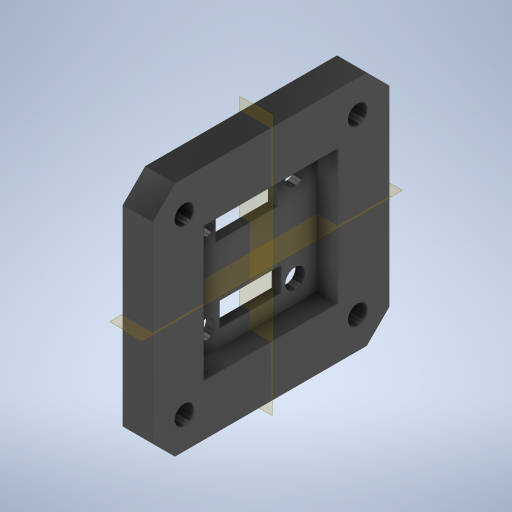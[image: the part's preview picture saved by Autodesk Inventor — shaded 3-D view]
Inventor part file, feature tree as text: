
AUTODESK INVENTOR PART (.ipt)
format: ipt  version: 2023 (Build 270158000, 158)  size: 315,392 bytes
history: native  units: mm
features: sketch x6, extrude x4, hole x2, chamfer x1
ambient origin geometry x8: Origin, YZ Plane, XZ Plane, XY Plane, X Axis, Y Axis, Z Axis, Center Point
bodies: Volumenkörper1 (feature_tree)
feature tree (13):
  extrude  "Extrusion1"  Depth=42.3mm
  extrude  "Extrusion2"  Depth=24.0mm
  hole  "Bohrung1"  [1 undecoded]
  hole  "Bohrung2"  [1 undecoded]
  chamfer  "Fase1"  Distance=8.0mm
  sketch  "Skizze5"  dims[d17=8.0mm]
  sketch  "Skizze6"  dims[d18=8.0mm d19=8.0mm d20=8.0mm d21=8.0mm d22=8.0mm d23=8.0mm d24=3.4mm d25=6.0mm d26=4.0mm d27=2.0mm d28=90.0deg d29=8.0mm d30=20.594885mm d31=15.5mm d32=15.5mm d33=15.5mm d34=15.5mm d35=15.5mm d36=15.5mm d37=15.5mm d38=15.5mm d39=4.0mm d40=2.0mm d41=45.0deg d42=11.0mm d43=4.3mm d44=3.0mm d45=5.8mm d46=11.0mm d47=4.3mm d48=3.0mm d49=5.5mm d50=10.0mm d51=0.0mm d52=10.0mm d53=0.0mm d54=0.5mm d55=0.872665mm d56=0.5mm d57=0.872665mm]
  extrude  "Extrusion3"  Depth=10.0mm
  extrude  "Extrusion4"  Depth=10.0mm
  sketch  "Skizze1"  dims[d0=42.3mm d1=42.3mm]
  sketch  "Skizze2"  dims[d2=5.3mm d3=0.0mm d4=24.0mm]
  sketch  "Skizze3"  dims[d5=24.0mm d6=3.7mm d7=0.0mm]
  sketch  "Skizze4"  dims[d9=3.5mm d10=6.0mm d11=4.0mm d12=2.0mm d13=90.0deg d14=8.0mm d15=20.594885mm d16=8.0mm]
note: 2 required parameter values undecoded (feature->parameter linkage not recoverable at this tier; creation-order binding heuristic only, values carry confidence <= 0.55)
